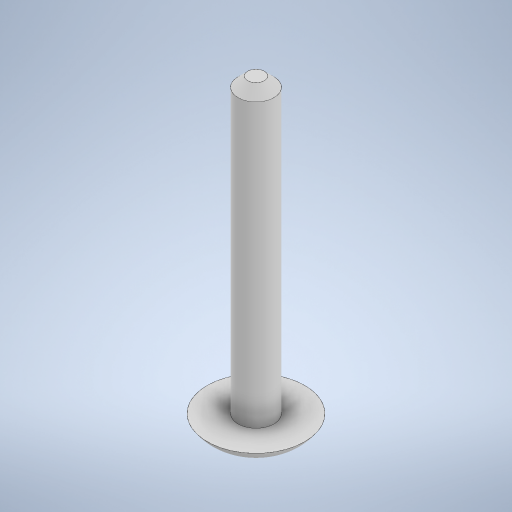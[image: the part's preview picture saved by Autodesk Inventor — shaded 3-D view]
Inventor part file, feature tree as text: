
AUTODESK INVENTOR PART (.ipt)
format: ipt  version: 2023 (Build 270158000, 158)  size: 246,272 bytes
history: native  units: mm
features: extrude x2, sketch x2, chamfer x1, fillet x1
ambient origin geometry x8: Origin, YZ Plane, XZ Plane, XY Plane, X Axis, Y Axis, Z Axis, Center Point
bodies: Solid1 (feature_tree)
feature tree (6):
  extrude  "Extrusion1"  Depth=30.0mm TaperAngle=0.0deg
  extrude  "Extrusion2"  Depth=2.0mm TaperAngle=0.0deg
  chamfer  "Chamfer1"  Distance=2.0mm Angle=45.0deg
  fillet  "Fillet1"  Radius=4.25mm
  sketch  "Sketch1"  dims[d0=3.7mm d1=30.0mm d2=0.0mm]
  sketch  "Sketch2"  dims[d3=10.0mm d4=2.0mm d5=0.0mm d6=1.0mm d7=2.0mm d8=45.0deg d12=4.25mm]
